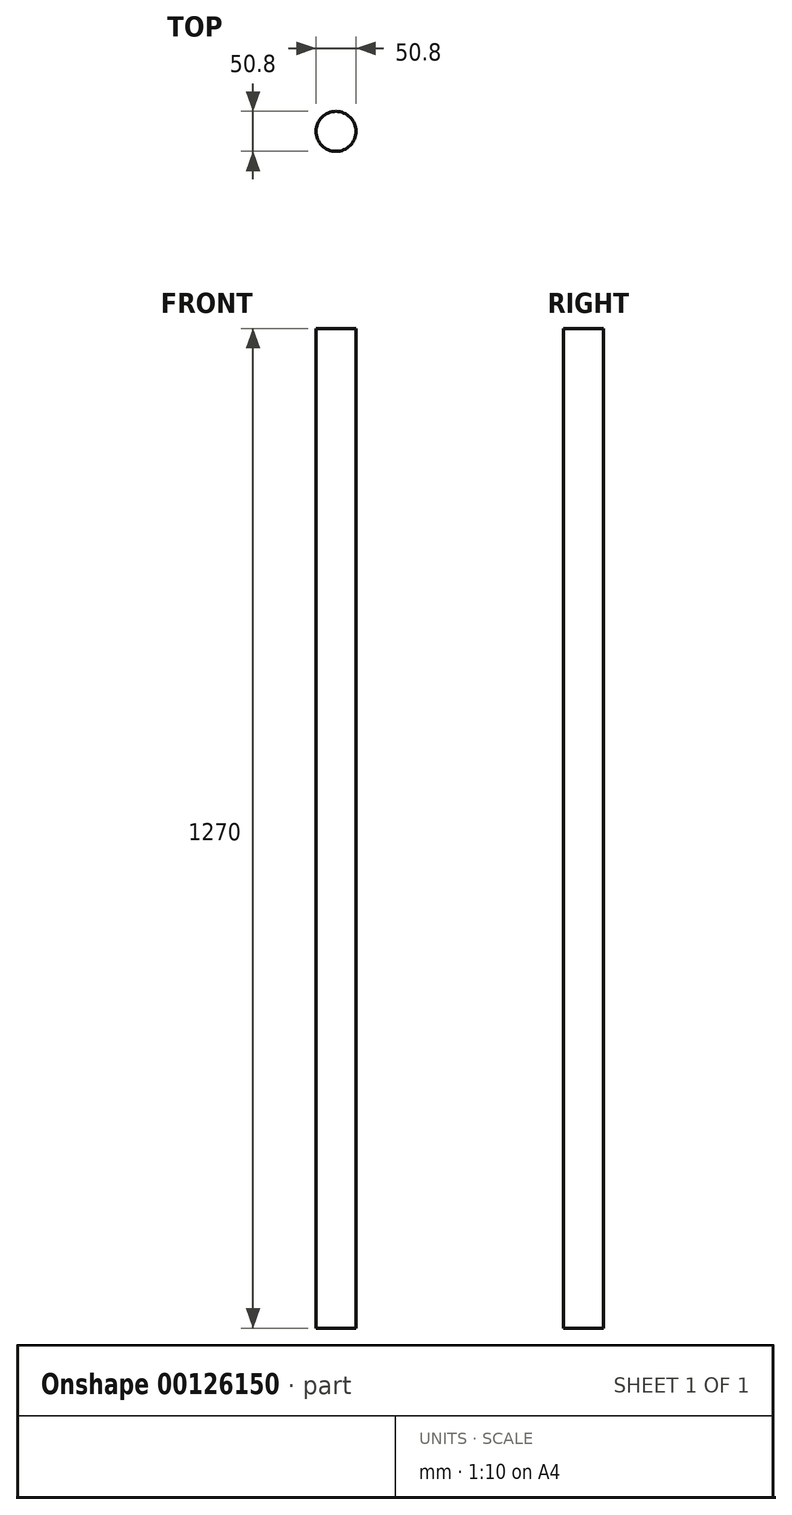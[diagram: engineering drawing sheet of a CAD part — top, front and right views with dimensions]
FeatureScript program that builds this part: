
annotation { "Feature Type Name" : "Feature", "Feature Type Description" : "" }
export const myFeature = defineFeature(function(context is Context, id is Id, definition is map)
    precondition{}
    {
        {
            var Q0;
            Q0=qCreatedBy(makeId("Top.planeOp"),FACE);
            var sketch = newSketch(context, id + "F0", { "sketchPlane" : qUnion([Q0])});
            skCircle(sketch, "E0", {"center": v(0, 0) * mm, "radius": 25.4 * mm});
            skSolve(sketch);
        }
        {
            var Q0;
            Q0 = qSketchRegion(id + "F0", true);
            extrude(context, id + "F1", {"entities" : qUnion([Q0]), "depth" : 1270 * mm});
        }
    });
